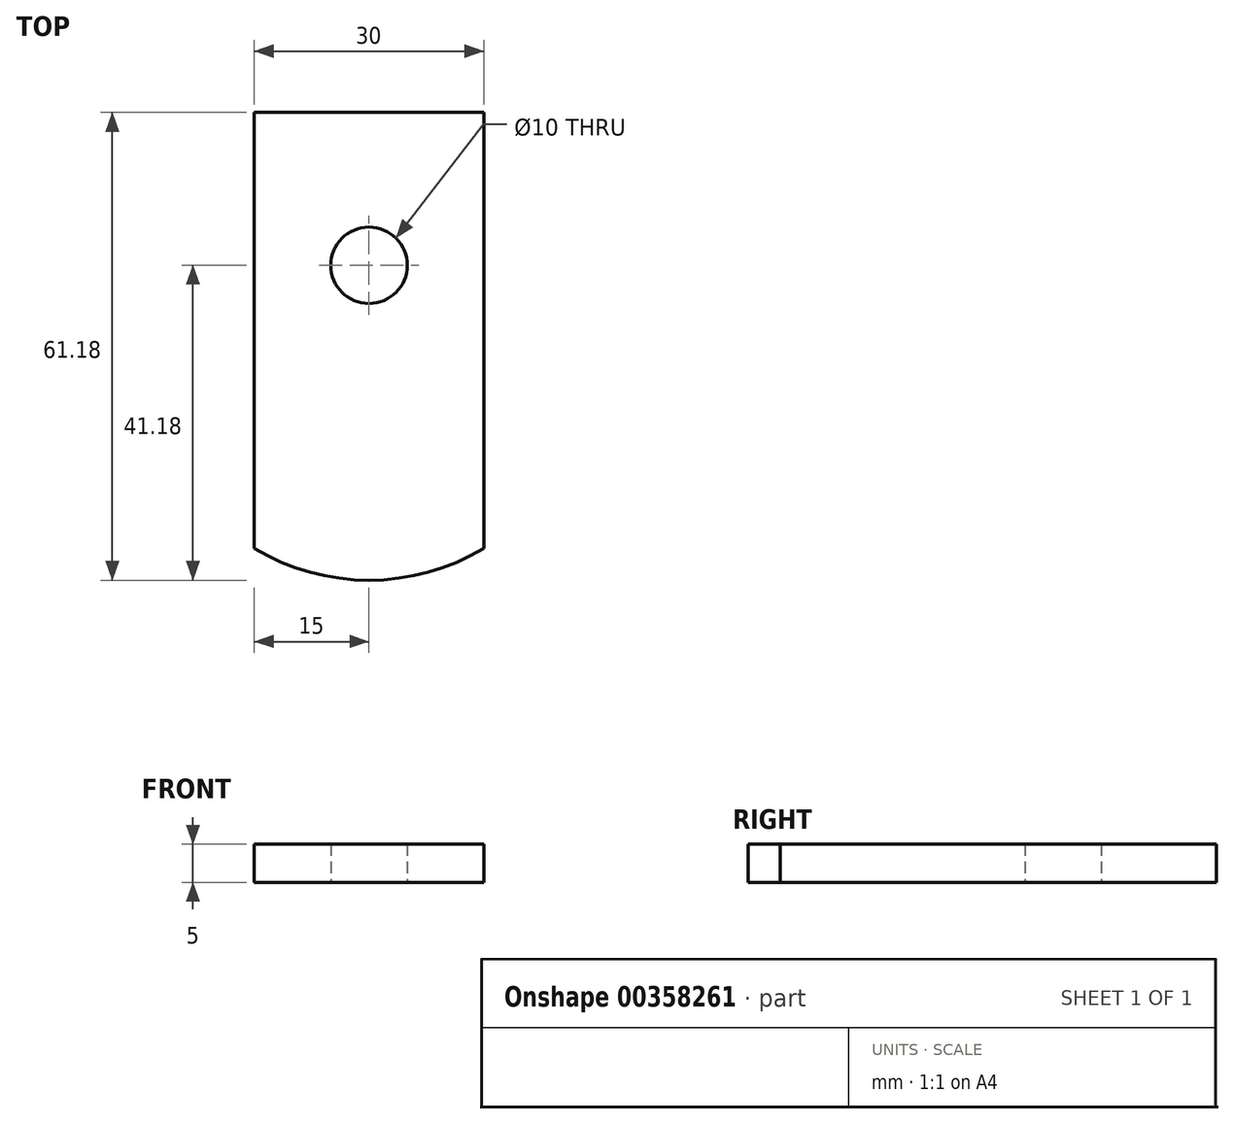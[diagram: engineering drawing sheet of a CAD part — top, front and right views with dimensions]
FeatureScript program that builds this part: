
annotation { "Feature Type Name" : "Feature", "Feature Type Description" : "" }
export const myFeature = defineFeature(function(context is Context, id is Id, definition is map)
    precondition{}
    {
        {
            var Q0;
            Q0=qCreatedBy(makeId("Top.planeOp"),FACE);
            var sketch = newSketch(context, id + "F0", { "sketchPlane" : qUnion([Q0])});
            skLineSegment(sketch, "E0.bottom", {"start": v(15, 28.5) * mm, "end": v(-15, 28.5) * mm});
            skLineSegment(sketch, "E0.left", {"start": v(15, 28.5) * mm, "end": v(15, -28.5) * mm});
            skLineSegment(sketch, "E0.right", {"start": v(-15, 28.5) * mm, "end": v(-15, -28.5) * mm});
            skPoint(sketch, "E0.middle", {"position": v(0, 0) * mm});
            skArc(sketch, "E1", {"start": v(-15, -28.5) * mm, "mid": v(0, -32.68) * mm, "end": v(15, -28.5) * mm});
            skCircle(sketch, "E2", {"center": v(0, 8.5) * mm, "radius": 5 * mm});
            skSolve(sketch);
        }
        {
            var Q0;
            Q0 = qSketchRegion(id + "F0", true);
            extrude(context, id + "F1", {"entities" : qUnion([Q0]), "depth" : 5 * mm});
        }
    });
